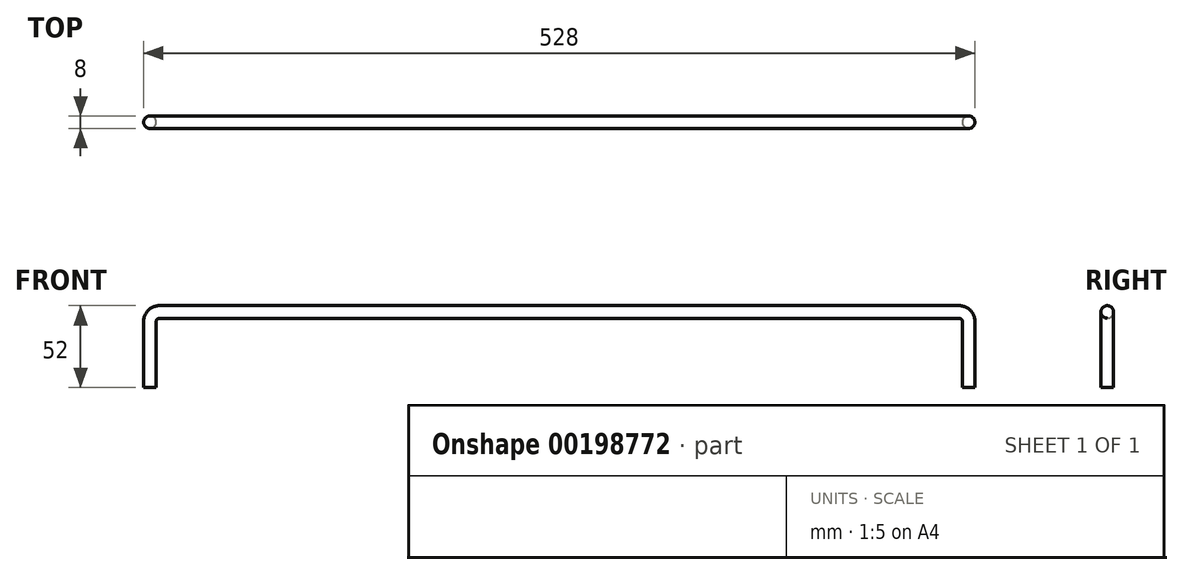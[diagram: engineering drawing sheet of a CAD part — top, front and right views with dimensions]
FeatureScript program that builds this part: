
annotation { "Feature Type Name" : "Feature", "Feature Type Description" : "" }
export const myFeature = defineFeature(function(context is Context, id is Id, definition is map)
    precondition{}
    {
        {
            var Q0;
            Q0=qCreatedBy(makeId("Front.planeOp"),FACE);
            var sketch = newSketch(context, id + "F0", { "sketchPlane" : qUnion([Q0])});
            skLineSegment(sketch, "E0.bottom", {"start": v(-260, 0) * mm, "end": v(260, 0) * mm, "construction": true});
            skLineSegment(sketch, "E0.top", {"start": v(-254, 48) * mm, "end": v(254, 48) * mm});
            skLineSegment(sketch, "E0.left", {"start": v(-260, 0) * mm, "end": v(-260, 42) * mm});
            skLineSegment(sketch, "E0.right", {"start": v(260, 0) * mm, "end": v(260, 42) * mm});
            skPoint(sketch, "E0.middle", {"position": v(0, 24) * mm});
            skPoint(sketch, "E1.visualSharp", {"position": v(-260, 48) * mm});
            skArc(sketch, "E1.filletArc", {"start": v(-254, 48) * mm, "mid": v(-258.24, 46.24) * mm, "end": v(-260, 42) * mm});
            skPoint(sketch, "E2.visualSharp", {"position": v(260, 48) * mm});
            skArc(sketch, "E2.filletArc", {"start": v(260, 42) * mm, "mid": v(258.24, 46.24) * mm, "end": v(254, 48) * mm});
            skSolve(sketch);
        }
        {
            var Q0;
            Q0=qCreatedBy(makeId("Top.planeOp"),FACE);
            var sketch = newSketch(context, id + "F1", { "sketchPlane" : qUnion([Q0])});
            skCircle(sketch, "E3", {"center": v(-260, 0) * mm, "radius": 4 * mm});
            skSolve(sketch);
        }
        {
            var Q0;
            Q0=makeQuery(id+"F1.imprint","IMPRINT",FACE,{"disambiguationData":[TD([[makeQuery(id+"F1.imprint","IMPRINT",EDGE,{"derivedFrom":sQuery(id+"F1.wireOp",EDGE,"E3")}),1.0]])]});
            var Q1;
            Q1=sQuery(id+"F0.wireOp",EDGE,"E0.left");
            var Q2;
            Q2=sQuery(id+"F0.wireOp",EDGE,"E1.filletArc");
            var Q3;
            Q3=sQuery(id+"F0.wireOp",EDGE,"E0.top");
            var Q4;
            Q4=sQuery(id+"F0.wireOp",EDGE,"E2.filletArc");
            var Q5;
            Q5=sQuery(id+"F0.wireOp",EDGE,"E0.right");
            sweep(context, id + "F2", {"profiles" : qUnion([Q0]), "path" : qUnion([Q1, Q2, Q3, Q4, Q5])});
        }
    });
